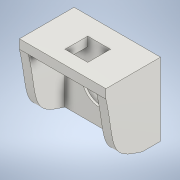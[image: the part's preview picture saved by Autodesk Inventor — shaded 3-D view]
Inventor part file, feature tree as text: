
AUTODESK INVENTOR PART (.ipt)
format: ipt  version: 2021 (Build 250183000, 183)  size: 186,368 bytes
history: native  units: mm
features: extrude x8, sketch x8, projected_geometry x4
ambient origin geometry x8: Origin, YZ Plane, XZ Plane, XY Plane, X Axis, Y Axis, Z Axis, Center Point
bodies: Solid1 (feature_tree)
feature tree (20):
  extrude  "Extrusion1"  Depth=30.0mm
  extrude  "Extrusion2"  Depth=15.0mm
  extrude  "Extrusion3"  Depth=2.0mm
  extrude  "Extrusion4"  Depth=10.0mm
  extrude  "Extrusion5"  Depth=10.0mm
  extrude  "Extrusion6"  Depth=2.0mm TaperAngle=0.0deg
  extrude  "Extrusion7"  Depth=4.0mm TaperAngle=0.0deg
  extrude  "Extrusion8"  [1 undecoded]
  sketch  "Sketch1"  dims[d0=22.2mm d1=30.0mm]
  sketch  "Sketch2"  dims[d2=7.0mm d3=0.0mm d4=15.0mm]
  projected_geometry  "Projected Loop1"
  sketch  "Sketch3"  dims[d5=1.0mm d6=0.0mm d7=2.0mm]
  sketch  "Sketch4"  dims[d8=10.0mm d9=0.0mm d10=10.0mm]
  sketch  "Sketch5"  dims[d11=10.0mm d12=10.0mm]
  projected_geometry  "Projected Loop2"
  sketch  "Sketch6"  dims[d13=10.0mm d14=0.0mm d15=2.0mm d16=0.0mm]
  sketch  "Sketch7"  dims[d17=6.0mm d18=0.0mm d19=4.0mm d20=0.0mm]
  projected_geometry  "Projected Loop3"
  sketch  "Sketch8"  dims[d21=4.0mm d22=0.0mm]
  projected_geometry  "Projected Loop4"
note: 1 required parameter value undecoded (feature->parameter linkage not recoverable at this tier; creation-order binding heuristic only, values carry confidence <= 0.55)
